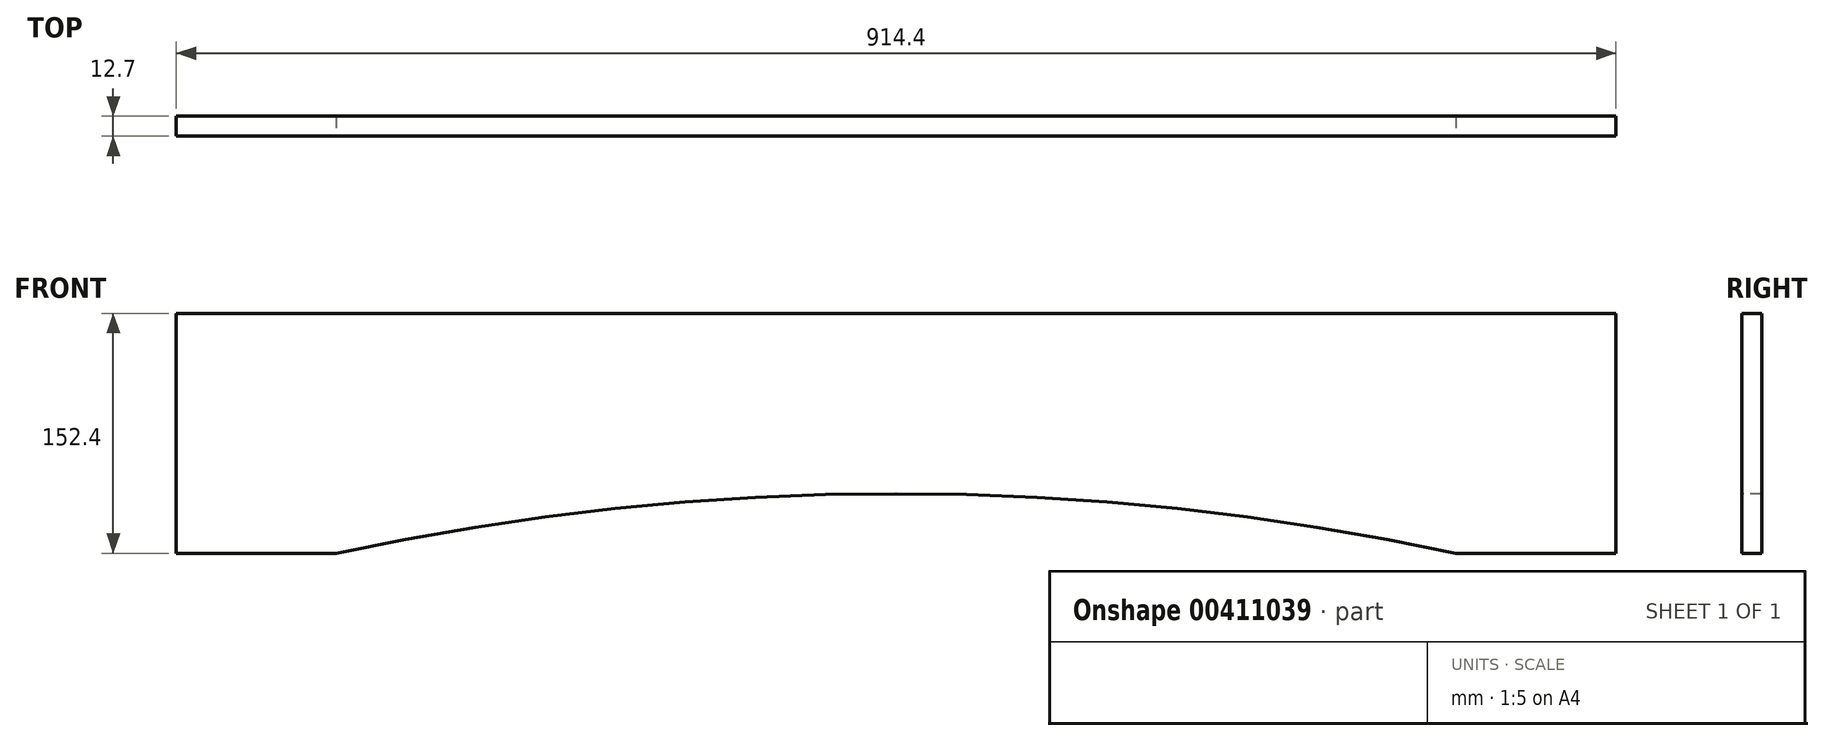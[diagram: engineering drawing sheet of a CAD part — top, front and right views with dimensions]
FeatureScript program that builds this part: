
annotation { "Feature Type Name" : "Feature", "Feature Type Description" : "" }
export const myFeature = defineFeature(function(context is Context, id is Id, definition is map)
    precondition{}
    {
        {
            var Q0;
            Q0=qCreatedBy(makeId("Front.planeOp"),FACE);
            var sketch = newSketch(context, id + "F0", { "sketchPlane" : qUnion([Q0])});
            skLineSegment(sketch, "E0", {"start": v(0, 0) * mm, "end": v(0, 152.4) * mm});
            skLineSegment(sketch, "E1", {"start": v(0, 152.4) * mm, "end": v(914.4, 152.4) * mm});
            skLineSegment(sketch, "E2", {"start": v(914.4, 152.4) * mm, "end": v(914.4, 0) * mm});
            skLineSegment(sketch, "E3", {"start": v(914.4, 0) * mm, "end": v(812.8, 0) * mm});
            skLineSegment(sketch, "E4", {"start": v(0, 0) * mm, "end": v(101.6, 0) * mm});
            skArc(sketch, "E5", {"start": v(812.8, 0) * mm, "mid": v(457.2, 37.8) * mm, "end": v(101.6, 0) * mm});
            skSolve(sketch);
        }
        {
            var Q0;
            Q0 = qSketchRegion(id + "F0", true);
            extrude(context, id + "F1", {"entities" : qUnion([Q0]), "oppositeDirection" : true, "depth" : 12.7 * mm});
        }
    });
